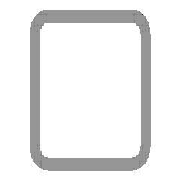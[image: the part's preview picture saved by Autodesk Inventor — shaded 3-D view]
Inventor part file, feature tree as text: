
AUTODESK INVENTOR PART (.ipt)
format: ipt  version: 2021 (Build 250183000, 183)  size: 143,360 bytes
history: native  units: mm (DEFAULTED — no unit token found)
features: other x5, sketch x3, extrude x1, split x1, plane x1
ambient origin geometry x8: Origin, YZ Plane, XZ Plane, XY Plane, X Axis, Y Axis, Z Axis, Center Point
bodies: Solid1 (feature_tree)
feature tree (11):
  parser-record x1  (decoder bookkeeping rows leaked as tree rows — omitted from the tree; the rows remain in map.json)
  other  "Driven Length"
  other  "Plano inicial"
  other  "Plano final"
  extrude  "Corpo"  TaperAngle=0.0deg  [1 undecoded]
  other  "Plano de trabalho4"
  split  "Dividir1"
  sketch  "Esboço"  dims[d11=50.8mm d12=4.7625mm d13=-21.334599mm d14=2236.067977mm d15=25.4mm d16=25.4mm d17=9.525mm d18=90.0deg d19=2257.402576mm]
  sketch  "Sketch3"  dims[d3=2255.402458mm d4=0.0mm]
  plane  "Work Plane3"
  sketch  "Sketch4"  dims[d10=50.8mm]
note: 1 required parameter value undecoded (feature->parameter linkage not recoverable at this tier; creation-order binding heuristic only, values carry confidence <= 0.55)
